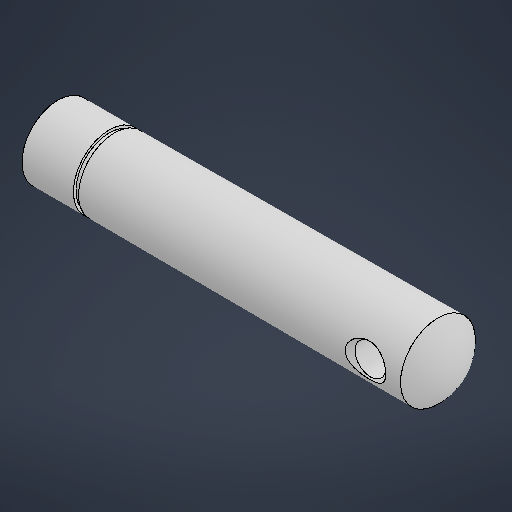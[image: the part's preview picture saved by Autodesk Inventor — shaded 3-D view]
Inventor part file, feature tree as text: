
AUTODESK INVENTOR PART (.ipt)
format: ipt  version: 2025.3 (Build 293356000, 356)  size: 243,200 bytes
history: native  units: mm
features: sketch x2, revolve x2, extrude x1, mirror x1
ambient origin geometry x8: Origin, YZ Plane, XZ Plane, XY Plane, X Axis, Y Axis, Z Axis, Center Point
bodies: Solid1 (feature_tree)
feature tree (6):
  sketch  "Sketch1"  dims[d4=0.043633mm d5=10.2mm]
  revolve  "Revolution1"  [1 undecoded]
  extrude  "Extrusion1"  Depth=10.0mm
  revolve  "Revolution2"  [1 undecoded]
  mirror  "Mirror1"
  sketch  "Sketch2"  dims[d6=14.0mm d7=14.0mm d11=50.0mm d13=60.0deg d19=10.0mm d20=77.0mm d21=67.0mm d22=6.0mm d23=0.5mm d24=10.0mm d25=1.0mm d26=90.0deg d27=0.0mm d28=0.0mm d29=45.0deg d30=1.0mm d31=90.0deg]
note: 2 required parameter values undecoded (feature->parameter linkage not recoverable at this tier; creation-order binding heuristic only, values carry confidence <= 0.55)
